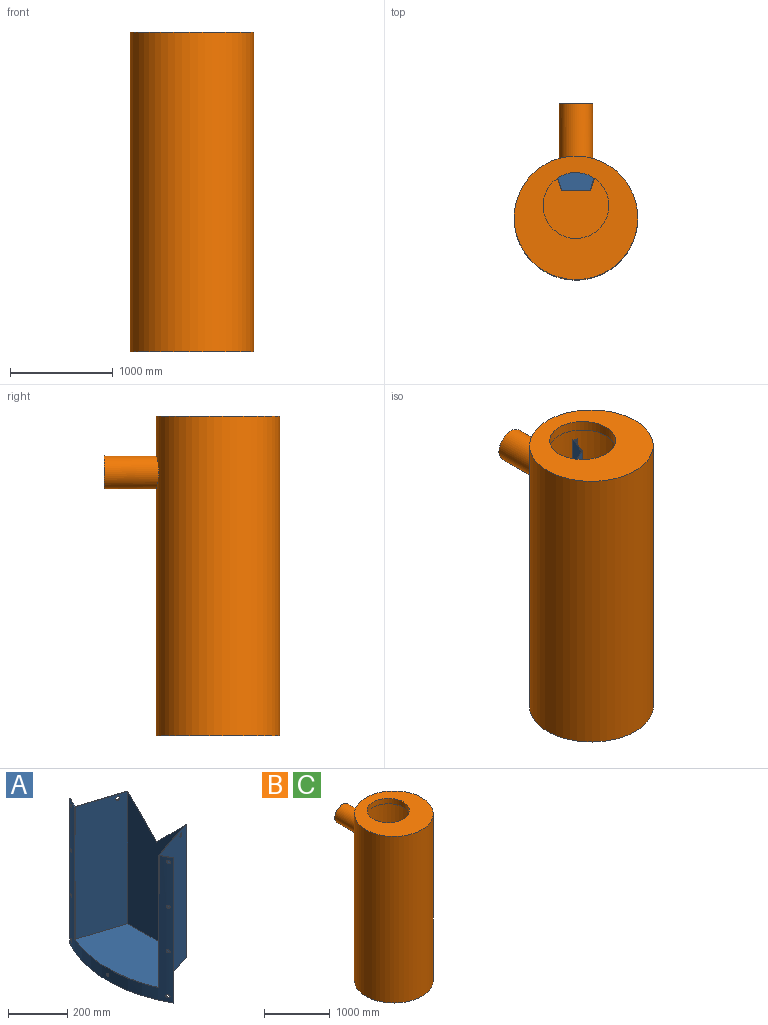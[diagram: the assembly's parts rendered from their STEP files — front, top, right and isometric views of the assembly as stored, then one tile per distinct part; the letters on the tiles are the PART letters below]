
ASSEMBLY  parts=3 mates=2
PART A: 34 faces, bbox 235x496.9x600 mm
  f0: cylinder r=500mm len=600mm, axis (0,0,-1), area 86025mm2, adj f2,f4,f5,f8,f13,f14,f15,f17
  f1: cylinder r=498mm len=600mm, axis (0,0,-1), area 82422.3mm2, adj f2,f3,f4,f5,f6,f8,f9,f12
  f2: plane 191.85x108.44mm, normal (0,0,1), area 503mm2, adj f0,f1,f5,f6,f10,f21,f31
  f3: plane 550x190.76mm, normal (0.3,0.95,0), area 109916.6mm2, adj f1,f4,f7,f9,f30,f32
  f4: plane 191.85x108.44mm, normal (0,0,1), area 503mm2, adj f0,f1,f3,f8,f11,f23,f30
  f5: plane 550x1.74mm, normal (0.5,-0.87,0), area 1100mm2, adj f0,f1,f2,f16
  f6: plane 550x190.76mm, normal (0.3,-0.95,0), area 109916.6mm2, adj f1,f2,f7,f9,f31,f33
  f7: plane 547.16x280mm, normal (1,0,0), area 133607.1mm2, adj f3,f6,f9,f30,f31
  f8: plane 550x1.74mm, normal (0.5,0.87,0), area 1100mm2, adj f0,f1,f4,f12
  f9: plane 401.42x233mm, normal (0,0,-1), area 76397.6mm2, adj f1,f3,f6,f7
  f10: plane 4.62x1.47mm, normal (0,0.71,0.71), area 4.8mm2, adj f2,f21,f31
  f11: plane 4.62x1.47mm, normal (0,-0.71,0.71), area 4.8mm2, adj f4,f23,f30
  f12: plane 1.74x0.99mm, normal (0,0,1), area 0mm2, adj f1,f8,f14
  f13: plane 50x1.74mm, normal (0.49,-0.87,0), area 100mm2, adj f0,f1,f15,f16
  f14: plane 50x1.74mm, normal (0.49,0.87,0), area 100mm2, adj f0,f1,f12,f15
  f15: plane 496.9x67.84mm, normal (0,0,-1), area 1038mm2, adj f0,f1,f13,f14
  f16: plane 1.74x0.99mm, normal (0,0,1), area 0mm2, adj f1,f5,f13
  f17: cylinder r=6mm len=12mm, axis (1,0,0), area 85mm2, adj f0,f1
  f18: cylinder r=6mm len=12mm, axis (1,0,0), area 85.1mm2, adj f0,f1
  f19: cylinder r=6mm len=12mm, axis (1,0,0), area 85.1mm2, adj f0,f1
  f20: cylinder r=6mm len=12mm, axis (1,0,0), area 85.2mm2, adj f0,f1
  f21: plane 548x191.49mm, normal (-0.3,0.95,0), area 109930.7mm2, adj f0,f2,f10,f22,f24,f33
  f22: plane 546.53x277.08mm, normal (-1,0,0), area 132238.4mm2, adj f21,f23,f24,f30,f31
  f23: plane 548x191.49mm, normal (-0.3,-0.95,0), area 109930.7mm2, adj f0,f4,f11,f22,f24,f32
  f24: plane 398.96x233mm, normal (0,0,1), area 75861.8mm2, adj f0,f21,f22,f23
  f25: cylinder r=6mm len=12mm, axis (1,0,0), area 85mm2, adj f0,f1
  f26: cylinder r=6mm len=12mm, axis (1,0,0), area 85.1mm2, adj f0,f1
  f27: cylinder r=6mm len=12mm, axis (1,0,0), area 85.2mm2, adj f0,f1
  f28: cylinder r=6mm len=12mm, axis (1,0,0), area 85.2mm2, adj f0,f1
  f29: cylinder r=5mm len=10mm, axis (1,0,0), area 62.8mm2, adj f0,f1
  f30: plane 142.83x140.52mm, normal (0.71,-0.5,0.5), area 561mm2, adj f3,f4,f7,f11,f22,f31
  f31: plane 142.83x140.52mm, normal (0.71,0.5,0.5), area 561mm2, adj f2,f6,f7,f10,f22,f30
  f32: cylinder r=7.5mm len=15mm, axis (0,1,0), area 98.9mm2, adj f3,f23
  f33: cylinder r=7.5mm len=15mm, axis (0,1,0), area 98.9mm2, adj f6,f21
PART B: 10 faces, bbox 1200x1708x3100 mm
  f0: cylinder r=157.5mm len=633.46mm, axis (0,-1,0), area 614198.6mm2, adj f5,f9
  f1: cylinder r=600mm len=3100mm, axis (0,0,-1), area 11602817.7mm2, adj f2,f3,f8
  f2: plane 1200x1200mm, normal (0,0,1), area 809274.3mm2, adj f1,f4
  f3: plane 1200x1200mm, normal (0,0,-1), area 1130973.4mm2, adj f1
  f4: cylinder r=320mm len=640mm, axis (0,0,1), area 201061.9mm2, adj f2,f6
  f5: cylinder r=500mm len=2900mm, axis (0,0,-1), area 9031764.6mm2, adj f0,f6,f7
  f6: plane 1000x1000mm, normal (0,0,-1), area 463699.1mm2, adj f4,f5
  f7: plane 1000x1000mm, normal (0,0,1), area 785398.2mm2, adj f5
  f8: cylinder r=162.5mm len=530.42mm, axis (0,-1,0), area 530089.3mm2, adj f1,f9
  f9: plane 325x325mm, normal (0,1,0), area 5026.5mm2, adj f0,f8
PART C: same geometry as B
PLACE A rot(axis=(0,0,-1),90deg) t=(0,0,2291)mm
PLACE B at identity fixed
PLACE C at identity
MATE cylindrical A.f0 <-> B.f1  axis (0,0,-1) through (0,0,2541)mm
MATE planar A.f2 <-> B.f1  axis (0,0,1) through (-181.63,380.46,2841)mm
